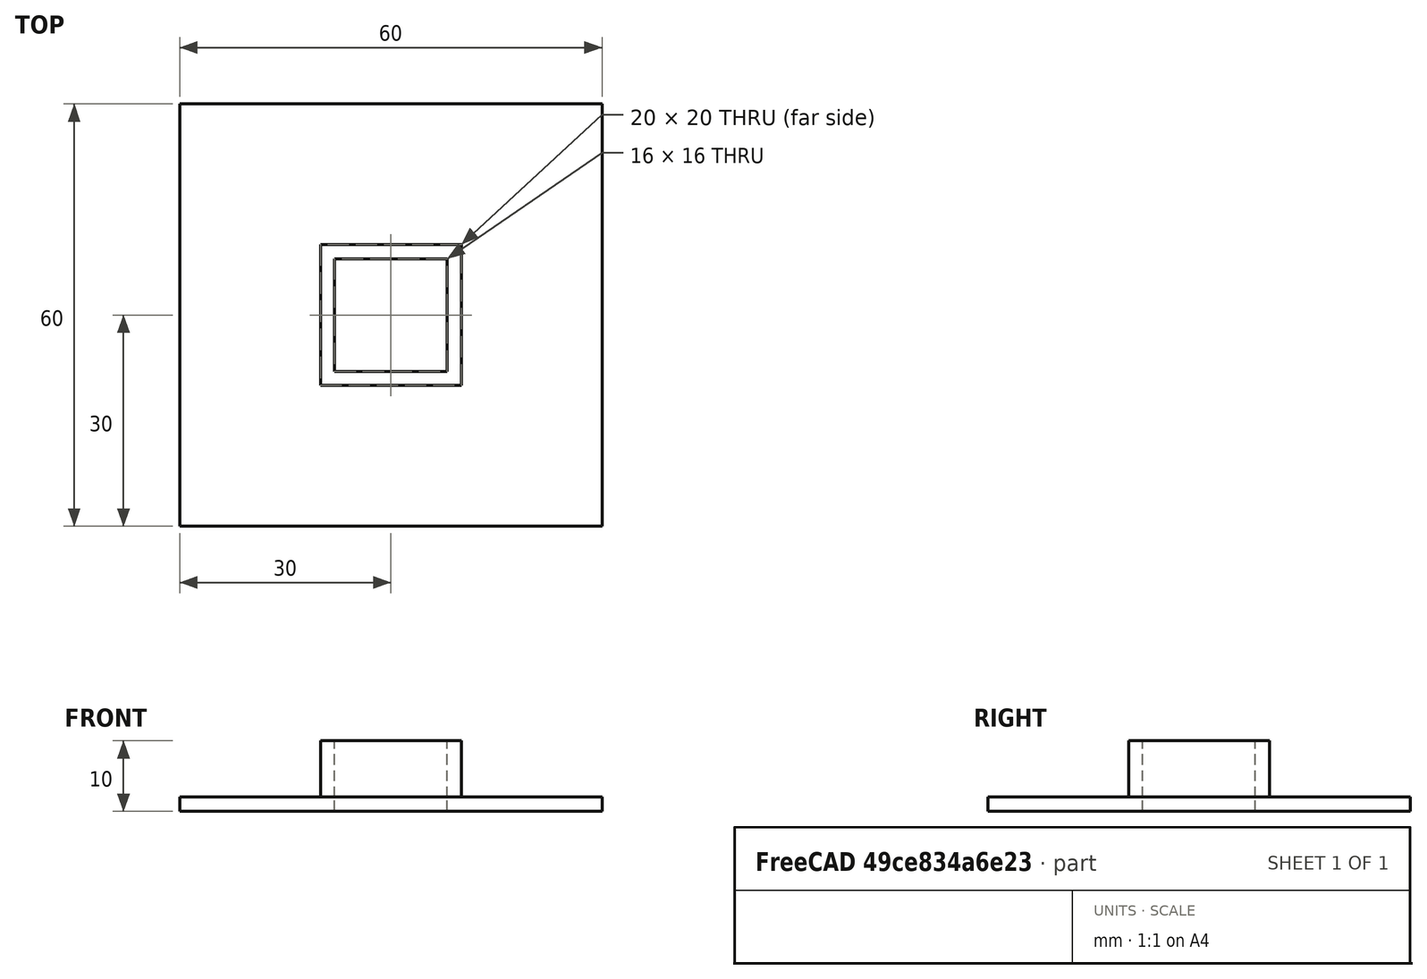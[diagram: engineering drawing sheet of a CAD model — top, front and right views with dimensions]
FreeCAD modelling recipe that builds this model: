
FCSTD DOCUMENT  (FreeCAD 0.17R13541 (Git))
Label: tactile_dataset_mount
License: All rights reserved
LicenseURL: http://en.wikipedia.org/wiki/All_rights_reserved
objects: Part::Box×4, Part::Cut×2, Part::Fuse×1
note: 7 computed .brp shape members not serialized (recipe doc carries the construction recipe); baked Part::Feature solids carry a one-line shape summary decoded from their .brp

FEATURE [Part::Box] Box  label="Cube"
  AttacherType = Attacher::AttachEngine3D
  Height = 2
  Length = 60
  Placement = pos=(-30,-30,0) rot=(0,0,1;0rad)
  Width = 60
FEATURE [Part::Box] Box001  label="Cube001"
  AttacherType = Attacher::AttachEngine3D
  Height = 3
  Length = 16
  Placement = pos=(-8,-8,0) rot=(0,0,1;0rad)
  Width = 16
FEATURE [Part::Cut] Cut
  Base = -> Box
  Tool = -> Box001
FEATURE [Part::Box] Box002  label="Cube002"
  AttacherType = Attacher::AttachEngine3D
  Height = 10
  Length = 16
  Placement = pos=(-8,-8,0) rot=(0,0,1;0rad)
  Width = 16
FEATURE [Part::Box] Box003  label="Cube003"
  AttacherType = Attacher::AttachEngine3D
  Height = 10
  Length = 20
  Placement = pos=(-10,-10,0) rot=(0,0,1;0rad)
  Width = 20
FEATURE [Part::Cut] Cut001
  Base = -> Box003
  Tool = -> Box002
FEATURE [Part::Fuse] Fusion
  Base = -> Cut
  Tool = -> Cut001
